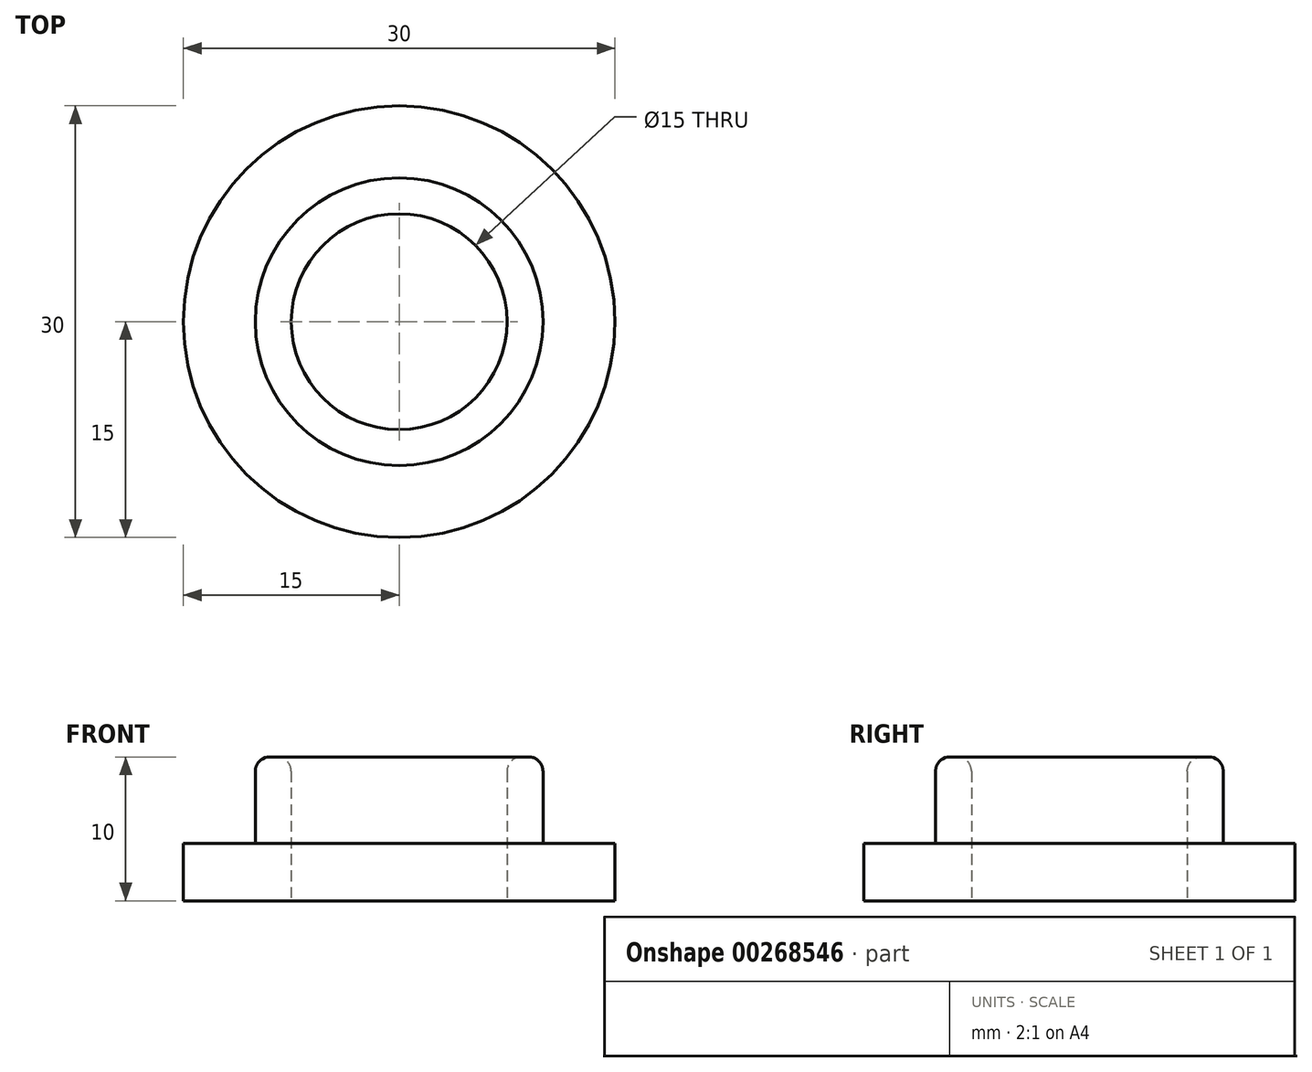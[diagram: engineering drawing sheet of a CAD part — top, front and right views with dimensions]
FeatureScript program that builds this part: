
annotation { "Feature Type Name" : "Feature", "Feature Type Description" : "" }
export const myFeature = defineFeature(function(context is Context, id is Id, definition is map)
    precondition{}
    {
        {
            var Q0;
            Q0=qCreatedBy(makeId("Top.planeOp"),FACE);
            var sketch = newSketch(context, id + "F0", { "sketchPlane" : qUnion([Q0])});
            skCircle(sketch, "E0", {"center": v(0, 0) * mm, "radius": 15 * mm});
            skCircle(sketch, "E1", {"center": v(0, 0) * mm, "radius": 7.5 * mm});
            skCircle(sketch, "E2", {"center": v(0, 0) * mm, "radius": 10 * mm});
            skSolve(sketch);
        }
        {
            var Q0;
            Q0=makeQuery(id+"F0.imprint","IMPRINT",FACE,{"disambiguationData":[TD([[makeQuery(id+"F0.imprint","IMPRINT",EDGE,{"derivedFrom":sQuery(id+"F0.wireOp",EDGE,"E0")}),1.0]])]});
            extrude(context, id + "F1", {"entities" : qUnion([Q0]), "depth" : 4 * mm});
        }
        {
            var Q0;
            Q0=makeQuery(id+"F0.imprint","IMPRINT",FACE,{"disambiguationData":[TD([[makeQuery(id+"F0.imprint","IMPRINT",EDGE,{"derivedFrom":sQuery(id+"F0.wireOp",EDGE,"E1")}),-1.0]])]});
            extrude(context, id + "F2", {"entities" : qUnion([Q0]), "operationType" : NewBodyOperationType.ADD, "depth" : 10 * mm});
        }
        {
            var Q0;
            Q0=makeQuery(id+"F2.opExtrude","CAP_EDGE",EDGE,{"disambiguationData":[OSD([sQuery(id+"F0.wireOp",EDGE,"E1")])],"isStart":false});
            var Q1;
            Q1=makeQuery(id+"F2.opExtrude","CAP_EDGE",EDGE,{"disambiguationData":[OSD([sQuery(id+"F0.wireOp",EDGE,"E2")])],"isStart":false});
            fillet(context, id + "F3", {"entities" : qUnion([Q0, Q1]), "radius" : 1 * mm, "tangentPropagation" : true, "allowEdgeOverflow" : false});
        }
    });
